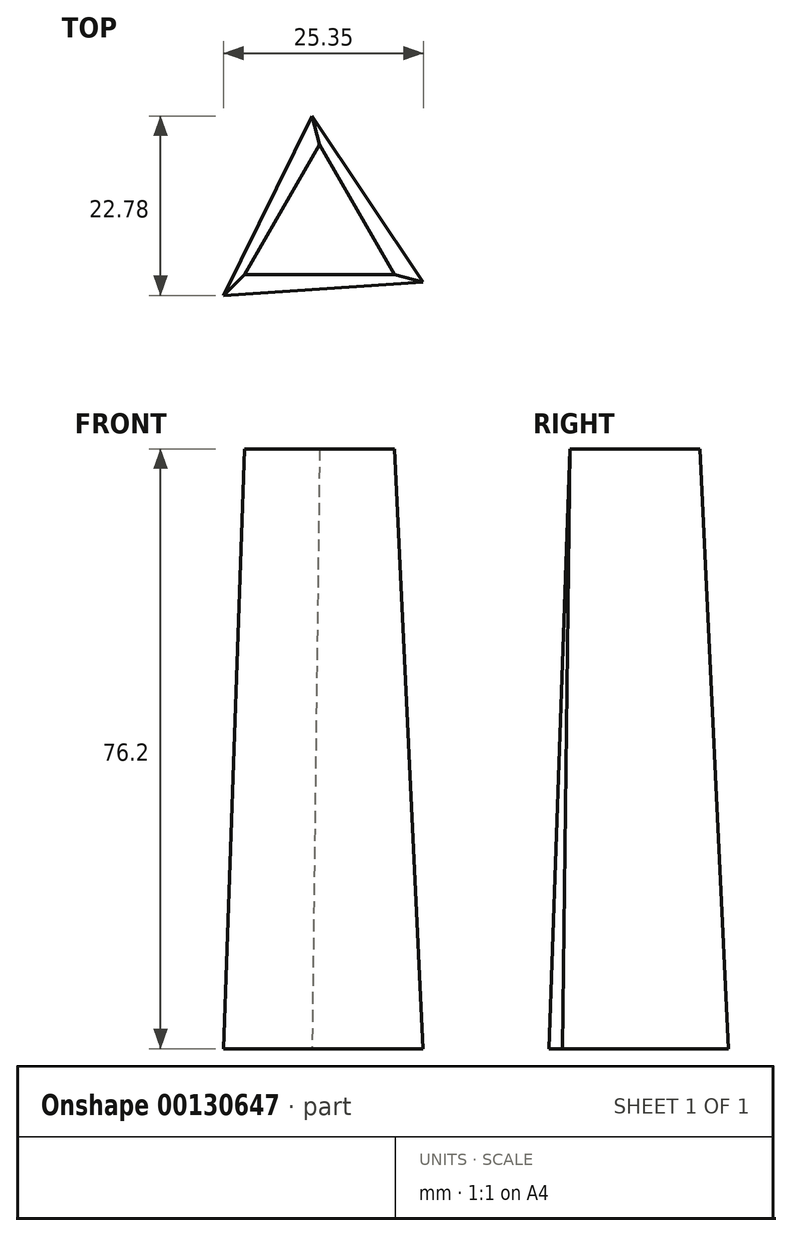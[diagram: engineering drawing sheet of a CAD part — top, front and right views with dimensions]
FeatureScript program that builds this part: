
annotation { "Feature Type Name" : "Feature", "Feature Type Description" : "" }
export const myFeature = defineFeature(function(context is Context, id is Id, definition is map)
    precondition{}
    {
        {
            var Q0;
            Q0=qCreatedBy(makeId("Top.planeOp"),FACE);
            var sketch = newSketch(context, id + "F0", { "sketchPlane" : qUnion([Q0])});
            skCircle(sketch, "E0.cCircle", {"center": v(0, 0) * mm, "radius": 7.33 * mm, "construction": true});
            skLineSegment(sketch, "E0.0", {"start": v(-0.97, 14.63) * mm, "end": v(13.16, -6.48) * mm});
            skLineSegment(sketch, "E0.1", {"start": v(13.16, -6.48) * mm, "end": v(-12.19, -8.15) * mm});
            skLineSegment(sketch, "E0.2", {"start": v(-12.19, -8.15) * mm, "end": v(-0.97, 14.63) * mm});
            skPoint(sketch, "E0.0.midPoint", {"position": v(6.1, 4.08) * mm});
            skSolve(sketch);
        }
        {
            var Q0;
            Q0=qCreatedBy(makeId("Top.planeOp"),FACE);
            cPlane(context, id + "F1", {"entities" : qUnion([Q0]), "cplaneType" : CPlaneType.OFFSET, "offset" : 76.2 * mm, "width" : 152.4 * mm, "height" : 152.4 * mm});
        }
        {
            var Q0;
            Q0=qCreatedBy(id+"F1.planeOp",FACE);
            var sketch = newSketch(context, id + "F2", { "sketchPlane" : qUnion([Q0])});
            skCircle(sketch, "E1.cCircle", {"center": v(0, 0) * mm, "radius": 5.5 * mm, "construction": true});
            skLineSegment(sketch, "E1.0", {"start": v(9.53, -5.5) * mm, "end": v(-9.53, -5.5) * mm});
            skLineSegment(sketch, "E1.1", {"start": v(-9.53, -5.5) * mm, "end": v(0, 11) * mm});
            skLineSegment(sketch, "E1.2", {"start": v(0, 11) * mm, "end": v(9.53, -5.5) * mm});
            skPoint(sketch, "E1.0.midPoint", {"position": v(0, -5.5) * mm});
            skSolve(sketch);
        }
        {
            var Q0;
            Q0=makeQuery(id+"F2.imprint","IMPRINT",FACE,{"disambiguationData":[TD([[makeQuery(id+"F2.imprint","IMPRINT",EDGE,{"derivedFrom":sQuery(id+"F2.wireOp",EDGE,"E1.0")}),-1.0]])]});
            var Q1;
            Q1=makeQuery(id+"F0.imprint","IMPRINT",FACE,{"disambiguationData":[TD([[makeQuery(id+"F0.imprint","IMPRINT",EDGE,{"derivedFrom":sQuery(id+"F0.wireOp",EDGE,"E0.0")}),-1.0]])]});
            loft(context, id + "F3", {"sheetProfilesArray" : [{ "sheetProfileEntities" : qUnion([Q0]) }, { "sheetProfileEntities" : qUnion([Q1]) }]});
        }
    });
